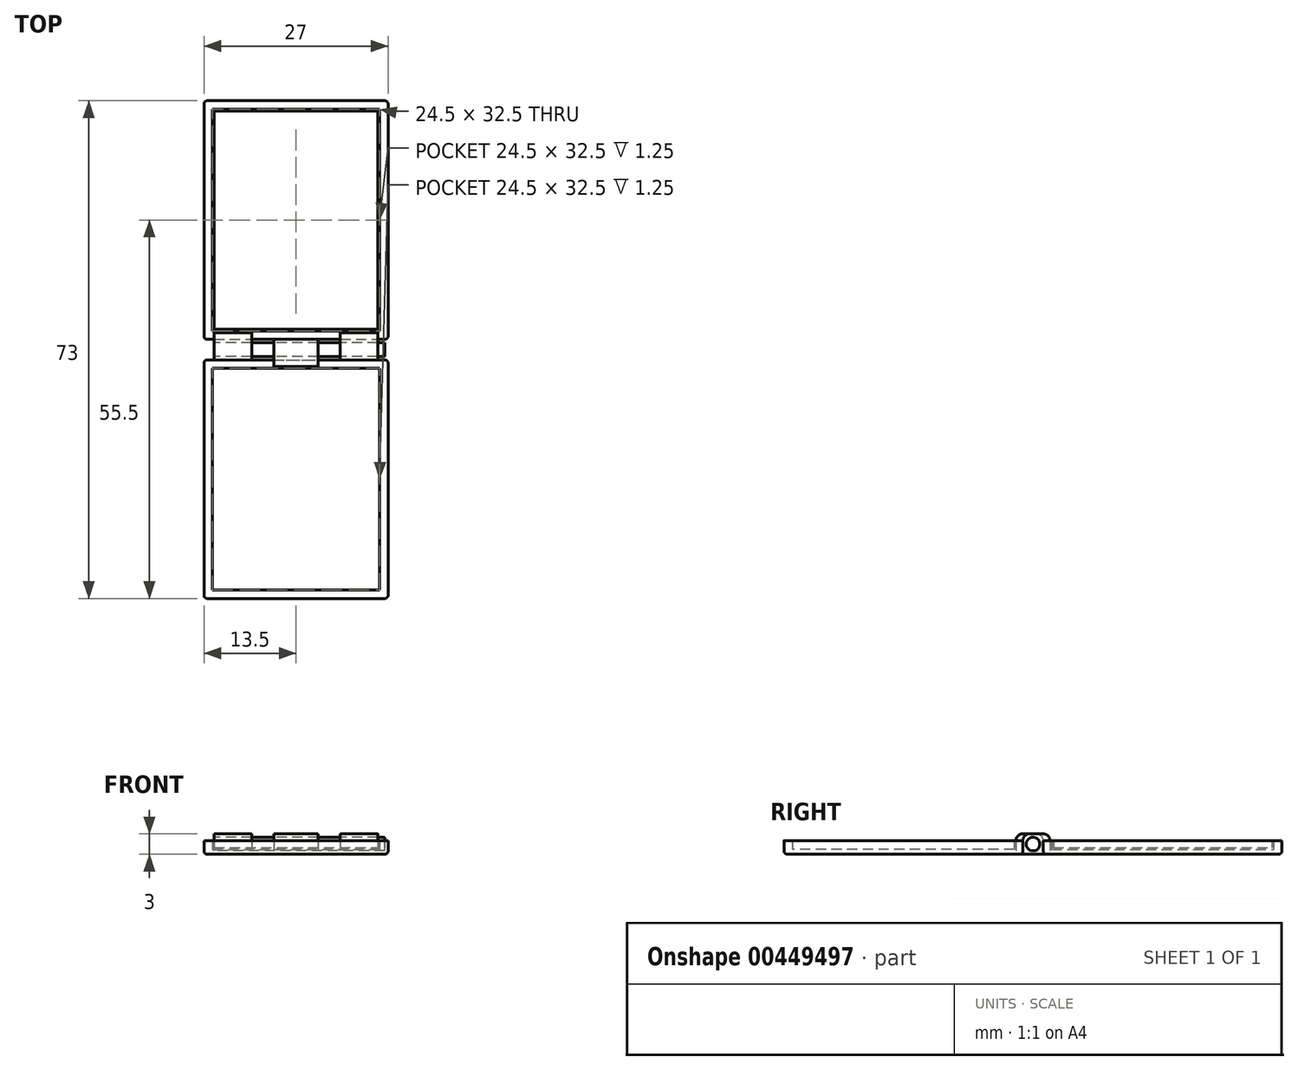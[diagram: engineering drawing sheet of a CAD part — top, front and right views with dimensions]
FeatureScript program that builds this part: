
annotation { "Feature Type Name" : "Feature", "Feature Type Description" : "" }
export const myFeature = defineFeature(function(context is Context, id is Id, definition is map)
    precondition{}
    {
        {
            var Q0;
            Q0=qCreatedBy(makeId("Top.planeOp"),FACE);
            var sketch = newSketch(context, id + "F0", { "sketchPlane" : qUnion([Q0])});
            skLineSegment(sketch, "E0.bottom", {"start": v(0, 0) * mm, "end": v(24, 0) * mm});
            skLineSegment(sketch, "E0.top", {"start": v(0, 32) * mm, "end": v(24, 32) * mm});
            skLineSegment(sketch, "E0.left", {"start": v(0, 0) * mm, "end": v(0, 32) * mm});
            skLineSegment(sketch, "E0.right", {"start": v(24, 0) * mm, "end": v(24, 32) * mm});
            skSolve(sketch);
        }
        {
            var Q0;
            Q0=makeQuery(id+"F0.imprint","IMPRINT",FACE,{"disambiguationData":[TD([[makeQuery(id+"F0.imprint","IMPRINT",EDGE,{"derivedFrom":sQuery(id+"F0.wireOp",EDGE,"E0.bottom")}),1.0]])]});
            extrude(context, id + "F1", {"entities" : qUnion([Q0]), "depth" : 2.1 * mm});
        }
        {
            var Q0;
            Q0=qCreatedBy(makeId("Top.planeOp"),FACE);
            cPlane(context, id + "F2", {"entities" : qUnion([Q0]), "cplaneType" : CPlaneType.OFFSET, "offset" : 1 * mm, "oppositeDirection" : true, "width" : 150 * mm, "height" : 150 * mm});
        }
        {
            var Q0;
            Q0=qCreatedBy(id+"F2.planeOp",FACE);
            var sketch = newSketch(context, id + "F3", { "sketchPlane" : qUnion([Q0])});
            skLineSegment(sketch, "E1.0.0", {"start": v(24, 32) * mm, "end": v(0, 32) * mm});
            skLineSegment(sketch, "E1.0.1", {"start": v(0, 32) * mm, "end": v(0, 0) * mm});
            skLineSegment(sketch, "E1.0.2", {"start": v(0, 0) * mm, "end": v(24, 0) * mm});
            skLineSegment(sketch, "E1.0.3", {"start": v(24, 0) * mm, "end": v(24, 32) * mm});
            skLineSegment(sketch, "E2.0", {"start": v(25.5, 33.5) * mm, "end": v(-1.5, 33.5) * mm});
            skLineSegment(sketch, "E2.1", {"start": v(25.5, -1.5) * mm, "end": v(25.5, 33.5) * mm});
            skLineSegment(sketch, "E2.2", {"start": v(-1.5, -1.5) * mm, "end": v(25.5, -1.5) * mm});
            skLineSegment(sketch, "E2.3", {"start": v(-1.5, 33.5) * mm, "end": v(-1.5, -1.5) * mm});
            skSolve(sketch);
        }
        {
            var Q0;
            Q0=makeQuery(id+"F3.imprint","IMPRINT",FACE,{"disambiguationData":[TD([[makeQuery(id+"F3.imprint","IMPRINT",EDGE,{"derivedFrom":sQuery(id+"F3.wireOp",EDGE,"E1.0.0")}),1.0]])]});
            var Q1;
            Q1=makeQuery(id+"F3.imprint","IMPRINT",FACE,{"disambiguationData":[TD([[makeQuery(id+"F3.imprint","IMPRINT",EDGE,{"derivedFrom":sQuery(id+"F3.wireOp",EDGE,"E1.0.0")}),-1.0]])]});
            extrude(context, id + "F4", {"entities" : qUnion([Q0, Q1]), "depth" : 4 * mm});
        }
        {
            var Q0;
            Q0=makeQuery(id+"F4.opExtrude","SWEPT_FACE",FACE,{"disambiguationData":[OSD([sQuery(id+"F3.wireOp",EDGE,"E2.1")])]});
            var sketch = newSketch(context, id + "F5", { "sketchPlane" : qUnion([Q0])});
            skPoint(sketch, "E3", {"position": v(-1.5, 1) * mm});
            skPoint(sketch, "E4", {"position": v(33.5, 1) * mm});
            skLineSegment(sketch, "E5.bottom", {"start": v(-1.5, 1) * mm, "end": v(33.5, 1) * mm});
            skLineSegment(sketch, "E5.top", {"start": v(-1.5, 3) * mm, "end": v(33.5, 3) * mm});
            skLineSegment(sketch, "E5.left", {"start": v(-1.5, 1) * mm, "end": v(-1.5, 3) * mm});
            skLineSegment(sketch, "E5.right", {"start": v(33.5, 1) * mm, "end": v(33.5, 3) * mm});
            skSolve(sketch);
        }
        {
            var Q0;
            Q0=makeQuery(id+"F1.opExtrude","SWEPT_BODY",BODY,{"disambiguationData":[OSD([sQuery(id+"F0.wireOp",EDGE,"E0.bottom"),sQuery(id+"F0.wireOp",EDGE,"E0.top"),sQuery(id+"F0.wireOp",EDGE,"E0.left"),sQuery(id+"F0.wireOp",EDGE,"E0.right")])]});
            var Q1;
            Q1=makeQuery(id+"F4.opExtrude","SWEPT_BODY",BODY,{"disambiguationData":[OSD([sQuery(id+"F3.wireOp",EDGE,"E2.0"),sQuery(id+"F3.wireOp",EDGE,"E2.1"),sQuery(id+"F3.wireOp",EDGE,"E2.2"),sQuery(id+"F3.wireOp",EDGE,"E2.3")])]});
            var Q2;
            Q2=makeQuery(id+"F1.opExtrude","SWEPT_FACE",FACE,{"disambiguationData":[OSD([sQuery(id+"F0.wireOp",EDGE,"E0.right")])]});
            var Q3;
            Q3=makeQuery(id+"F1.opExtrude","SWEPT_FACE",FACE,{"disambiguationData":[OSD([sQuery(id+"F0.wireOp",EDGE,"E0.left")])]});
            booleanBodies(context, id + "F6", {"operationType" : BooleanOperationType.SUBTRACTION, "tools" : qUnion([Q0]), "targets" : qUnion([Q1]), "offset" : true, "offsetAll" : true, "entitiesToOffset" : qUnion([Q2, Q3]), "offsetDistance" : 0.25 * mm, "keepTools" : true});
        }
        {
            var Q0;
            Q0=makeQuery(id+"F4.opExtrude","SWEPT_EDGE",EDGE,{"disambiguationData":[OSD([sQuery(id+"F3.wireOp",EDGE,"E2.2"),sQuery(id+"F3.wireOp",EDGE,"E2.3")])]});
            var Q1;
            Q1=makeQuery(id+"F4.opExtrude","SWEPT_EDGE",EDGE,{"disambiguationData":[OSD([sQuery(id+"F3.wireOp",EDGE,"E2.1"),sQuery(id+"F3.wireOp",EDGE,"E2.2")])]});
            var Q2;
            Q2=makeQuery(id+"F4.opExtrude","SWEPT_EDGE",EDGE,{"disambiguationData":[OSD([sQuery(id+"F3.wireOp",EDGE,"E2.0"),sQuery(id+"F3.wireOp",EDGE,"E2.1")])]});
            var Q3;
            Q3=makeQuery(id+"F4.opExtrude","SWEPT_EDGE",EDGE,{"disambiguationData":[OSD([sQuery(id+"F3.wireOp",EDGE,"E2.0"),sQuery(id+"F3.wireOp",EDGE,"E2.3")])]});
            var Q4;
            Q4=makeQuery(id+"F4.opExtrude","CAP_EDGE",EDGE,{"disambiguationData":[OSD([sQuery(id+"F3.wireOp",EDGE,"E2.3")])],"isStart":false});
            var Q5;
            Q5=makeQuery(id+"F4.opExtrude","CAP_EDGE",EDGE,{"disambiguationData":[OSD([sQuery(id+"F3.wireOp",EDGE,"E2.0")])],"isStart":false});
            var Q6;
            Q6=makeQuery(id+"F4.opExtrude","CAP_EDGE",EDGE,{"disambiguationData":[OSD([sQuery(id+"F3.wireOp",EDGE,"E2.0")])],"isStart":true});
            var Q7;
            Q7=makeQuery(id+"F4.opExtrude","CAP_EDGE",EDGE,{"disambiguationData":[OSD([sQuery(id+"F3.wireOp",EDGE,"E2.3")])],"isStart":true});
            var Q8;
            Q8=makeQuery(id+"F4.opExtrude","CAP_EDGE",EDGE,{"disambiguationData":[OSD([sQuery(id+"F3.wireOp",EDGE,"E2.1")])],"isStart":false});
            var Q9;
            Q9=makeQuery(id+"F4.opExtrude","CAP_EDGE",EDGE,{"disambiguationData":[OSD([sQuery(id+"F3.wireOp",EDGE,"E2.1")])],"isStart":true});
            var Q10;
            Q10=makeQuery(id+"F4.opExtrude","CAP_EDGE",EDGE,{"disambiguationData":[OSD([sQuery(id+"F3.wireOp",EDGE,"E2.2")])],"isStart":false});
            var Q11;
            Q11=makeQuery(id+"F4.opExtrude","CAP_EDGE",EDGE,{"disambiguationData":[OSD([sQuery(id+"F3.wireOp",EDGE,"E2.2")])],"isStart":true});
            fillet(context, id + "F7", {"entities" : qUnion([Q0, Q1, Q2, Q3, Q4, Q5, Q6, Q7, Q8, Q9, Q10, Q11]), "radius" : 0.5 * mm, "tangentPropagation" : true, "allowEdgeOverflow" : false});
        }
        {
            var Q0;
            Q0=makeQuery(id+"F5.imprint","IMPRINT",FACE,{"disambiguationData":[TD([[makeQuery(id+"F5.imprint","IMPRINT",EDGE,{"derivedFrom":sQuery(id+"F5.wireOp",EDGE,"E5.bottom")}),1.0]])]});
            var Q1;
            Q1=makeQuery(id+"F4.opExtrude","SWEPT_FACE",FACE,{"disambiguationData":[OSD([sQuery(id+"F3.wireOp",EDGE,"E2.3")])]});
            extrude(context, id + "F8", {"entities" : qUnion([Q0]), "operationType" : NewBodyOperationType.REMOVE, "endBound" : BoundingType.UP_TO_SURFACE, "oppositeDirection" : true, "endBoundEntityFace" : qUnion([Q1]), "depth" : 25 * mm});
        }
        {
            var Q0;
            Q0=qCreatedBy(makeId("Front.planeOp"),FACE);
            cPlane(context, id + "F9", {"entities" : qUnion([Q0]), "cplaneType" : CPlaneType.OFFSET, "offset" : 3 * mm, "width" : 150 * mm, "height" : 150 * mm});
        }
        {
            var Q0;
            Q0=makeQuery(id+"F4.opExtrude","SWEPT_BODY",BODY,{"disambiguationData":[OSD([sQuery(id+"F3.wireOp",EDGE,"E2.0"),sQuery(id+"F3.wireOp",EDGE,"E2.1"),sQuery(id+"F3.wireOp",EDGE,"E2.2"),sQuery(id+"F3.wireOp",EDGE,"E2.3")])]});
            var Q1;
            Q1=qCreatedBy(id+"F9.planeOp",FACE);
            mirror(context, id + "F10", {"entities" : qUnion([Q0]), "mirrorPlane" : qUnion([Q1])});
        }
        {
            var Q0;
            Q0=qCreatedBy(id+"F2.planeOp",FACE);
            var sketch = newSketch(context, id + "F11", { "sketchPlane" : qUnion([Q0])});
            skLineSegment(sketch, "E6.0", {"start": v(-1, -1.5) * mm, "end": v(25, -1.5) * mm, "construction": true});
            skLineSegment(sketch, "E7.0", {"start": v(-1, -4.5) * mm, "end": v(25, -4.5) * mm, "construction": true});
            skLineSegment(sketch, "E8", {"start": v(-1, -1.5) * mm, "end": v(-1, -4.5) * mm, "construction": true});
            skLineSegment(sketch, "E9", {"start": v(25, -4.5) * mm, "end": v(25, -1.5) * mm, "construction": true});
            skPoint(sketch, "E10", {"position": v(12, -1.5) * mm});
            skPoint(sketch, "E11", {"position": v(12, -4.5) * mm});
            skPoint(sketch, "E12", {"position": v(-1, -3) * mm});
            skPoint(sketch, "E13", {"position": v(25, -3) * mm});
            skLineSegment(sketch, "E14", {"start": v(12, -1.5) * mm, "end": v(12, -4.5) * mm, "construction": true});
            skPoint(sketch, "E15", {"position": v(12, -3) * mm});
            skLineSegment(sketch, "E16", {"start": v(-1, -3) * mm, "end": v(12, -3) * mm, "construction": true});
            skLineSegment(sketch, "E17", {"start": v(12, -3) * mm, "end": v(25, -3) * mm, "construction": true});
            skPoint(sketch, "E18", {"position": v(5.5, -3) * mm});
            skPoint(sketch, "E19", {"position": v(18.5, -3) * mm});
            skLineSegment(sketch, "E20", {"start": v(18.5, -3) * mm, "end": v(18.5, -4.5) * mm, "construction": true});
            skLineSegment(sketch, "E21", {"start": v(18.5, -4.5) * mm, "end": v(18.5, -3) * mm, "construction": true});
            skLineSegment(sketch, "E22", {"start": v(18.5, -1.5) * mm, "end": v(18.5, -3) * mm, "construction": true});
            skLineSegment(sketch, "E23", {"start": v(5.5, -3) * mm, "end": v(5.5, -4.5) * mm, "construction": true});
            skLineSegment(sketch, "E24", {"start": v(5.5, -4.5) * mm, "end": v(5.5, -3) * mm, "construction": true});
            skLineSegment(sketch, "E25", {"start": v(5.5, -1.5) * mm, "end": v(5.5, -3) * mm, "construction": true});
            skLineSegment(sketch, "E26.bottom", {"start": v(-1, -1.5) * mm, "end": v(5.5, -1.5) * mm});
            skLineSegment(sketch, "E26.top", {"start": v(-1, -4.5) * mm, "end": v(5.5, -4.5) * mm});
            skLineSegment(sketch, "E26.left", {"start": v(-1, -1.5) * mm, "end": v(-1, -4.5) * mm});
            skLineSegment(sketch, "E26.right", {"start": v(5.5, -1.5) * mm, "end": v(5.5, -4.5) * mm});
            skLineSegment(sketch, "E27.bottom", {"start": v(18.5, -1.5) * mm, "end": v(25, -1.5) * mm});
            skLineSegment(sketch, "E27.top", {"start": v(18.5, -4.5) * mm, "end": v(25, -4.5) * mm});
            skLineSegment(sketch, "E27.left", {"start": v(18.5, -1.5) * mm, "end": v(18.5, -4.5) * mm});
            skLineSegment(sketch, "E27.right", {"start": v(25, -1.5) * mm, "end": v(25, -4.5) * mm});
            skLineSegment(sketch, "E28.bottom", {"start": v(8.75, -1.5) * mm, "end": v(15.25, -1.5) * mm});
            skLineSegment(sketch, "E28.top", {"start": v(8.75, -4.5) * mm, "end": v(15.25, -4.5) * mm});
            skLineSegment(sketch, "E28.left", {"start": v(8.75, -1.5) * mm, "end": v(8.75, -4.5) * mm});
            skLineSegment(sketch, "E28.right", {"start": v(15.25, -1.5) * mm, "end": v(15.25, -4.5) * mm});
            skPoint(sketch, "E29", {"position": v(25, -1.5) * mm});
            skLineSegment(sketch, "E30", {"start": v(18.5, -1.5) * mm, "end": v(18.5, -0.5) * mm});
            skLineSegment(sketch, "E31", {"start": v(5.5, -1.5) * mm, "end": v(5.5, -0.5) * mm});
            skLineSegment(sketch, "E32", {"start": v(8.75, -1.5) * mm, "end": v(8.75, -0.5) * mm});
            skLineSegment(sketch, "E33", {"start": v(15.25, -1.5) * mm, "end": v(15.25, -0.5) * mm});
            skLineSegment(sketch, "E34", {"start": v(0, -5.5) * mm, "end": v(5.5, -5.5) * mm});
            skLineSegment(sketch, "E35", {"start": v(5.5, -4.5) * mm, "end": v(5.5, -5.5) * mm});
            skLineSegment(sketch, "E36", {"start": v(8.75, -4.5) * mm, "end": v(8.75, -5.5) * mm});
            skLineSegment(sketch, "E37", {"start": v(15.25, -4.5) * mm, "end": v(15.25, -5.5) * mm});
            skLineSegment(sketch, "E38", {"start": v(18.5, -4.5) * mm, "end": v(18.5, -5.5) * mm});
            skPoint(sketch, "E39", {"position": v(0, -0.5) * mm});
            skPoint(sketch, "E40", {"position": v(24, -0.5) * mm});
            skPoint(sketch, "E41", {"position": v(24, -5.5) * mm});
            skPoint(sketch, "E42", {"position": v(0, -5.5) * mm});
            skLineSegment(sketch, "E43", {"start": v(24, -5.5) * mm, "end": v(24, -1.5) * mm});
            skPoint(sketch, "E44", {"position": v(0, -1.5) * mm});
            skPoint(sketch, "E45", {"position": v(24, -1.5) * mm});
            skPoint(sketch, "E46", {"position": v(24, -4.5) * mm});
            skPoint(sketch, "E47", {"position": v(0, -4.5) * mm});
            skLineSegment(sketch, "E48", {"start": v(24, -1.5) * mm, "end": v(24, -0.5) * mm});
            skLineSegment(sketch, "E49", {"start": v(18.5, -1.5) * mm, "end": v(24, -1.5) * mm});
            skLineSegment(sketch, "E50", {"start": v(0, -1.5) * mm, "end": v(5.5, -1.5) * mm});
            skPoint(sketch, "E51", {"position": v(-1, -0.5) * mm});
            skPoint(sketch, "E52", {"position": v(25, -0.5) * mm});
            skLineSegment(sketch, "E53", {"start": v(0, -0.5) * mm, "end": v(5.5, -0.5) * mm});
            skLineSegment(sketch, "E54", {"start": v(18.5, -0.5) * mm, "end": v(24, -0.5) * mm});
            skLineSegment(sketch, "E55.trimOffspring", {"start": v(8.75, -5.5) * mm, "end": v(15.25, -5.5) * mm});
            skLineSegment(sketch, "E56.trimOffspring", {"start": v(18.5, -5.5) * mm, "end": v(24, -5.5) * mm});
            skLineSegment(sketch, "E57", {"start": v(8.75, -0.5) * mm, "end": v(15.25, -0.5) * mm});
            skLineSegment(sketch, "E58", {"start": v(0, -1.5) * mm, "end": v(0, -0.5) * mm});
            skLineSegment(sketch, "E59", {"start": v(0, -5.5) * mm, "end": v(0, -4.5) * mm});
            skLineSegment(sketch, "E60", {"start": v(0, -1.5) * mm, "end": v(0, -4.5) * mm});
            skSolve(sketch);
        }
        {
            var Q0;
            Q0=makeQuery(id+"F11.imprint","IMPRINT",FACE,{"disambiguationData":[TD([[makeQuery(id+"F11.imprint","IMPRINT",EDGE,{"derivedFrom":sQuery(id+"F11.wireOp",EDGE,"E28.bottom")}),-1.0]])]});
            var Q1;
            {var subQ0=sQuery(id+"F11.wireOp",EDGE,"E27.left");Q1=makeQuery(id+"F11.imprint","IMPRINT",FACE,{"disambiguationData":[TD([[makeQuery(id+"F11.imprint","IMPRINT",EDGE,{"derivedFrom":subQ0}),1.0]])]});}
            var Q2;
            Q2=makeQuery(id+"F11.imprint","IMPRINT",FACE,{"disambiguationData":[TD([[makeQuery(id+"F11.imprint","IMPRINT",EDGE,{"derivedFrom":sQuery(id+"F11.wireOp",EDGE,"E30")}),-1.0]])]});
            var Q3;
            Q3=makeQuery(id+"F11.imprint","IMPRINT",FACE,{"disambiguationData":[TD([[makeQuery(id+"F11.imprint","IMPRINT",EDGE,{"derivedFrom":sQuery(id+"F11.wireOp",EDGE,"E28.top")}),-1.0]])]});
            var Q4;
            Q4=makeQuery(id+"F11.imprint","IMPRINT",FACE,{"disambiguationData":[TD([[makeQuery(id+"F11.imprint","IMPRINT",EDGE,{"derivedFrom":sQuery(id+"F11.wireOp",EDGE,"E31")}),1.0]])]});
            var Q5;
            {var subQ0=sQuery(id+"F11.wireOp",EDGE,"E26.right");Q5=makeQuery(id+"F11.imprint","IMPRINT",FACE,{"disambiguationData":[TD([[makeQuery(id+"F11.imprint","IMPRINT",EDGE,{"derivedFrom":subQ0}),-1.0]])]});}
            extrude(context, id + "F12", {"entities" : qUnion([Q0, Q1, Q2, Q3, Q4, Q5]), "depth" : 3 * mm});
        }
        {
            var Q0;
            Q0=makeQuery(id+"F12.opExtrude","SWEPT_FACE",FACE,{"disambiguationData":[OSD([sQuery(id+"F11.wireOp",EDGE,"E58"),sQuery(id+"F11.wireOp",EDGE,"E60")])]});
            var sketch = newSketch(context, id + "F13", { "sketchPlane" : qUnion([Q0])});
            skPoint(sketch, "E61", {"position": v(3, 0.5) * mm});
            skCircle(sketch, "E62", {"center": v(3, 0.5) * mm, "radius": 1 * mm});
            skPoint(sketch, "E63", {"position": v(0.5, 0.5) * mm});
            skPoint(sketch, "E64", {"position": v(3, 2) * mm});
            skSolve(sketch);
        }
        {
            var Q0;
            Q0=qSketchRegion(id+"F13",true);
            extrude(context, id + "F14", {"entities" : qUnion([Q0]), "oppositeDirection" : true, "depth" : 25 * mm});
        }
        {
            var Q0;
            Q0=makeQuery(id+"F12.opExtrude","CAP_EDGE",EDGE,{"disambiguationData":[OSD([sQuery(id+"F11.wireOp",EDGE,"E56.trimOffspring")])],"isStart":false});
            var Q1;
            Q1=makeQuery(id+"F12.opExtrude","CAP_EDGE",EDGE,{"disambiguationData":[OSD([sQuery(id+"F11.wireOp",EDGE,"E55.trimOffspring")])],"isStart":false});
            var Q2;
            Q2=makeQuery(id+"F12.opExtrude","CAP_EDGE",EDGE,{"disambiguationData":[OSD([sQuery(id+"F11.wireOp",EDGE,"E34")])],"isStart":false});
            var Q3;
            Q3=makeQuery(id+"F12.opExtrude","CAP_EDGE",EDGE,{"disambiguationData":[OSD([sQuery(id+"F11.wireOp",EDGE,"E53")])],"isStart":false});
            var Q4;
            Q4=makeQuery(id+"F12.opExtrude","CAP_EDGE",EDGE,{"disambiguationData":[OSD([sQuery(id+"F11.wireOp",EDGE,"E57")])],"isStart":false});
            var Q5;
            Q5=makeQuery(id+"F12.opExtrude","CAP_EDGE",EDGE,{"disambiguationData":[OSD([sQuery(id+"F11.wireOp",EDGE,"E54")])],"isStart":false});
            var Q6;
            Q6=makeQuery(id+"F12.opExtrude","CAP_EDGE",EDGE,{"disambiguationData":[OSD([sQuery(id+"F11.wireOp",EDGE,"E27.top")])],"isStart":false});
            var Q7;
            Q7=makeQuery(id+"F12.opExtrude","CAP_EDGE",EDGE,{"disambiguationData":[OSD([sQuery(id+"F11.wireOp",EDGE,"E26.top")])],"isStart":false});
            var Q8;
            Q8=makeQuery(id+"F12.opExtrude","CAP_EDGE",EDGE,{"disambiguationData":[OSD([sQuery(id+"F11.wireOp",EDGE,"E28.bottom")])],"isStart":false});
            fillet(context, id + "F15", {"entities" : qUnion([Q0, Q1, Q2, Q3, Q4, Q5, Q6, Q7, Q8]), "radius" : 1 * mm, "tangentPropagation" : true, "allowEdgeOverflow" : false});
        }
        {
            var Q0;
            Q0=makeQuery(id+"F4.opExtrude","SWEPT_BODY",BODY,{"disambiguationData":[OSD([sQuery(id+"F3.wireOp",EDGE,"E2.0"),sQuery(id+"F3.wireOp",EDGE,"E2.1"),sQuery(id+"F3.wireOp",EDGE,"E2.2"),sQuery(id+"F3.wireOp",EDGE,"E2.3")])]});
            transform(context, id + "F16", {"entities" : qUnion([Q0]), "transformType" : TransformType.TRANSLATION_3D, "dx" : 0 * mm, "dy" : 0 * mm, "dz" : 0 * mm, "makeCopy" : true});
        }
        {
            var Q0;
            Q0=makeQuery(id+"F4.opExtrude","SWEPT_BODY",BODY,{"disambiguationData":[OSD([sQuery(id+"F3.wireOp",EDGE,"E2.0"),sQuery(id+"F3.wireOp",EDGE,"E2.1"),sQuery(id+"F3.wireOp",EDGE,"E2.2"),sQuery(id+"F3.wireOp",EDGE,"E2.3")])]});
            transform(context, id + "F17", {"entities" : qUnion([Q0]), "transformType" : TransformType.TRANSLATION_3D, "dx" : 0 * mm, "dy" : 0 * mm, "dz" : 0 * mm, "makeCopy" : true});
        }
    });
